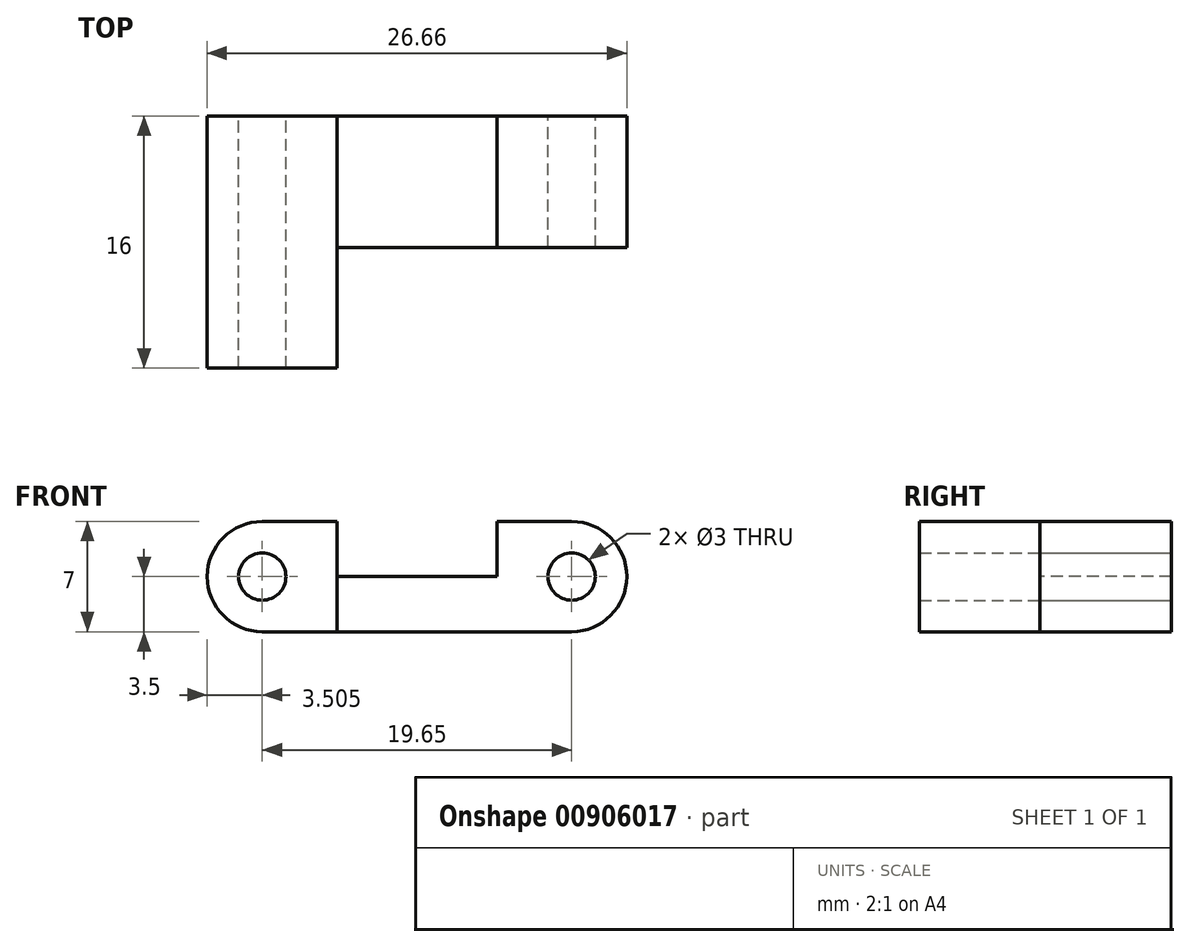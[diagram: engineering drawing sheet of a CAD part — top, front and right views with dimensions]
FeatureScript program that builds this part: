
annotation { "Feature Type Name" : "Feature", "Feature Type Description" : "" }
export const myFeature = defineFeature(function(context is Context, id is Id, definition is map)
    precondition{}
    {
        {
            var Q0;
            Q0=qCreatedBy(makeId("Front.planeOp"),FACE);
            var sketch = newSketch(context, id + "F0", { "sketchPlane" : qUnion([Q0])});
            skArc(sketch, "E0", {"start": v(-9.82, 3.5) * mm, "mid": v(-13.32, 0) * mm, "end": v(-9.82, -3.5) * mm});
            skArc(sketch, "E1", {"start": v(9.82, -3.5) * mm, "mid": v(13.32, 0) * mm, "end": v(9.83, 3.5) * mm});
            skLineSegment(sketch, "E2", {"start": v(-9.82, 3.5) * mm, "end": v(9.83, 3.5) * mm});
            skLineSegment(sketch, "E3", {"start": v(9.83, -3.5) * mm, "end": v(-9.82, -3.5) * mm});
            skCircle(sketch, "E4", {"center": v(9.83, 0) * mm, "radius": 1.5 * mm});
            skCircle(sketch, "E5", {"center": v(-9.82, 0) * mm, "radius": 1.5 * mm});
            skSolve(sketch);
        }
        {
            var Q0;
            Q0=qSketchRegion(id+"F0",true);
            extrude(context, id + "F1", {"entities" : qUnion([Q0]), "endBound" : BoundingType.SYMMETRIC, "depth" : 16 * mm, "offsetDistance" : 25.4 * mm});
        }
        {
            var Q0;
            Q0=makeQuery(id+"F1.opExtrude","SWEPT_FACE",FACE,{"disambiguationData":[OSD([sQuery(id+"F0.wireOp",EDGE,"E2")])]});
            var sketch = newSketch(context, id + "F2", { "sketchPlane" : qUnion([Q0])});
            skLineSegment(sketch, "E6.bottom", {"start": v(25.15, -14.92) * mm, "end": v(-5.08, -14.92) * mm});
            skLineSegment(sketch, "E6.top", {"start": v(25.15, -0.35) * mm, "end": v(-5.08, -0.35) * mm});
            skLineSegment(sketch, "E6.left", {"start": v(25.15, -14.92) * mm, "end": v(25.15, -0.35) * mm});
            skLineSegment(sketch, "E6.right", {"start": v(-5.08, -14.92) * mm, "end": v(-5.08, -0.35) * mm});
            skSolve(sketch);
        }
        {
            var Q0;
            Q0=qSketchRegion(id+"F2",true);
            extrude(context, id + "F3", {"entities" : qUnion([Q0]), "operationType" : NewBodyOperationType.REMOVE, "oppositeDirection" : true, "depth" : 25.4 * mm, "offsetDistance" : 25.4 * mm});
        }
        {
            var Q0;
            Q0=makeQuery(id+"F3.boolean.opBoolean","COPY",FACE,{"derivedFrom":makeQuery(id+"F3.opExtrude","SWEPT_FACE",FACE,{"disambiguationData":[OSD([sQuery(id+"F2.wireOp",EDGE,"E6.top")])]})});
            var sketch = newSketch(context, id + "F4", { "sketchPlane" : qUnion([Q0])});
            skLineSegment(sketch, "E7.bottom", {"start": v(-5.08, 6.53) * mm, "end": v(5.08, 6.53) * mm});
            skLineSegment(sketch, "E7.top", {"start": v(-5.08, 0) * mm, "end": v(5.08, 0) * mm});
            skLineSegment(sketch, "E7.left", {"start": v(-5.08, 6.53) * mm, "end": v(-5.08, 0) * mm});
            skLineSegment(sketch, "E7.right", {"start": v(5.08, 6.53) * mm, "end": v(5.08, 0) * mm});
            skSolve(sketch);
        }
        {
            var Q0;
            Q0=qSketchRegion(id+"F4",true);
            extrude(context, id + "F5", {"entities" : qUnion([Q0]), "operationType" : NewBodyOperationType.REMOVE, "oppositeDirection" : true, "depth" : 25.4 * mm, "offsetDistance" : 25.4 * mm});
        }
    });
